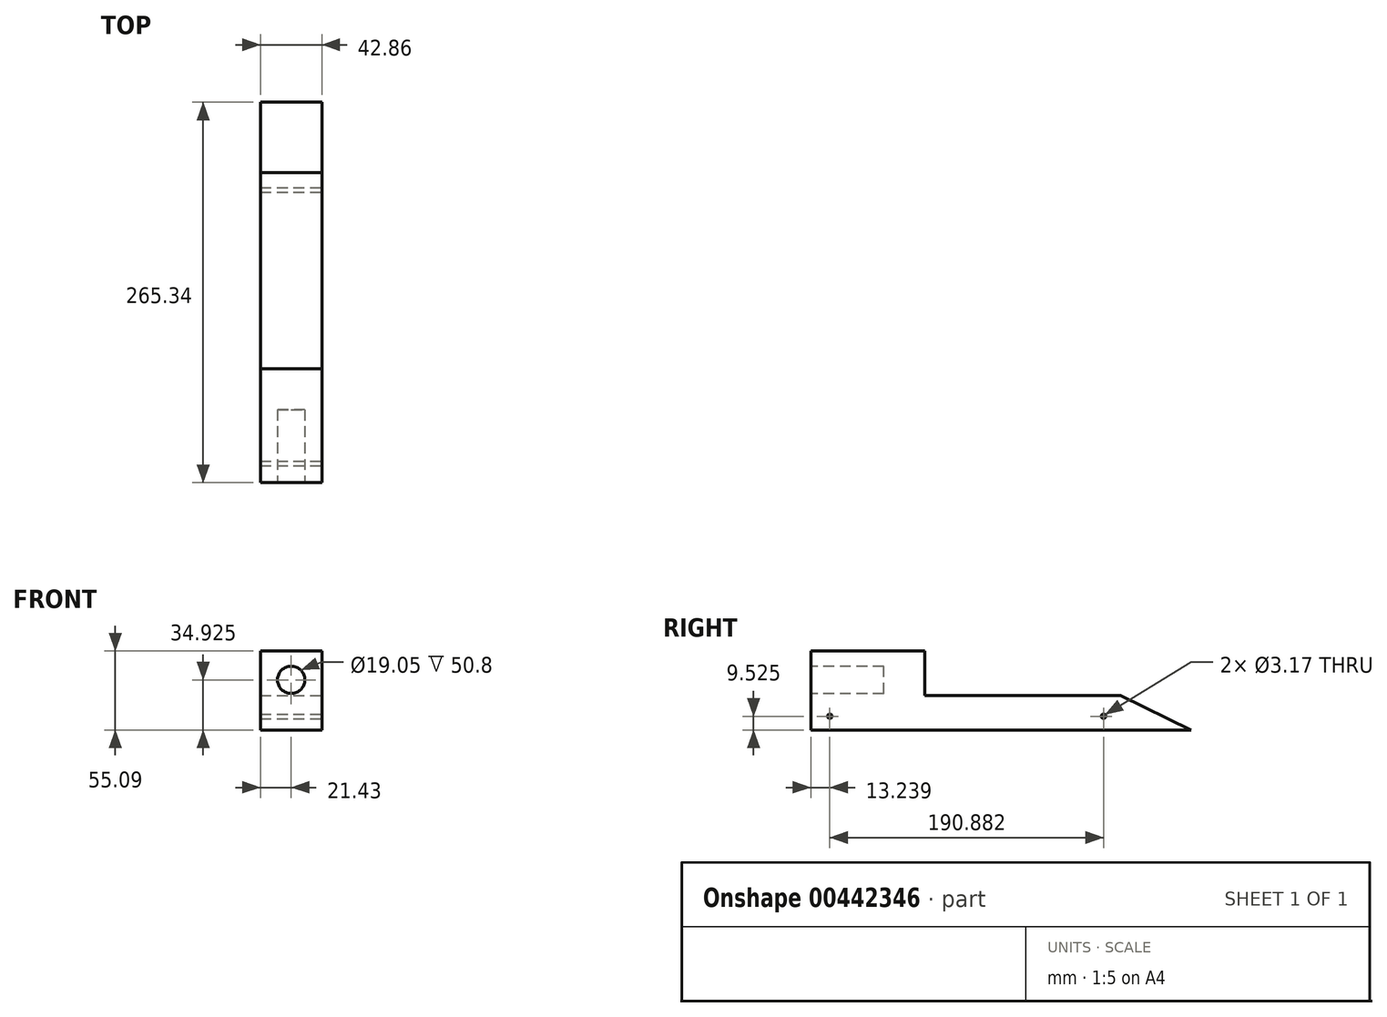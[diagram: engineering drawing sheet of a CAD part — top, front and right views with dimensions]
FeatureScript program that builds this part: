
annotation { "Feature Type Name" : "Feature", "Feature Type Description" : "" }
export const myFeature = defineFeature(function(context is Context, id is Id, definition is map)
    precondition{}
    {
        {
            var Q0;
            Q0=qCreatedBy(makeId("Right.planeOp"),FACE);
            var sketch = newSketch(context, id + "F0", { "sketchPlane" : qUnion([Q0])});
            skLineSegment(sketch, "E0", {"start": v(-152.4, 0) * mm, "end": v(152.4, 0) * mm});
            skLineSegment(sketch, "E1", {"start": v(-152.4, 0) * mm, "end": v(-152.4, 69.85) * mm});
            skLineSegment(sketch, "E2", {"start": v(152.4, 0) * mm, "end": v(152.4, 19.05) * mm});
            skLineSegment(sketch, "E3", {"start": v(152.4, 19.05) * mm, "end": v(-152.4, 69.85) * mm});
            skPoint(sketch, "E4.endSnap0", {"position": v(-152.4, 34.93) * mm});
            skLineSegment(sketch, "E5.0", {"start": v(-95.25, 50.8) * mm, "end": v(-152.4, 50.8) * mm, "construction": true});
            skLineSegment(sketch, "E5.1", {"start": v(-95.25, 50.8) * mm, "end": v(-95.25, 19.05) * mm, "construction": true});
            skLineSegment(sketch, "E5.2", {"start": v(-95.25, 19.05) * mm, "end": v(-152.4, 19.05) * mm, "construction": true});
            skSolve(sketch);
        }
        {
            var Q0;
            Q0=makeQuery(id+"F0.imprint","IMPRINT",FACE,{"disambiguationData":[TD([[makeQuery(id+"F0.imprint","IMPRINT",EDGE,{"derivedFrom":sQuery(id+"F0.wireOp",EDGE,"E0")}),1.0]])]});
            extrude(context, id + "F1", {"entities" : qUnion([Q0]), "depth" : 42.86 * mm, "symmetric" : true});
        }
        {
            var Q0;
            Q0=makeQuery(id+"F1.opExtrude","SWEPT_FACE",FACE,{"disambiguationData":[OSD([sQuery(id+"F0.wireOp",EDGE,"E1")])]});
            var sketch = newSketch(context, id + "F2", { "sketchPlane" : qUnion([Q0])});
            skLineSegment(sketch, "E6", {"start": v(21.43, 34.93) * mm, "end": v(0, 34.93) * mm, "construction": true});
            skCircle(sketch, "E7", {"center": v(0, 34.93) * mm, "radius": 9.53 * mm});
            skSolve(sketch);
        }
        {
            var Q0;
            Q0=makeQuery(id+"F2.imprint","IMPRINT",FACE,{"disambiguationData":[TD([[makeQuery(id+"F2.imprint","IMPRINT",EDGE,{"derivedFrom":sQuery(id+"F2.wireOp",EDGE,"E7")}),1.0]])]});
            var Q1;
            Q1=sQuery(id+"F2.wireOp",EDGE,"E7");
            extrude(context, id + "F3", {"entities" : qUnion([Q0]), "operationType" : NewBodyOperationType.REMOVE, "surfaceEntities" : qUnion([Q1]), "oppositeDirection" : true, "depth" : 50.8 * mm});
        }
        {
            var Q0;
            Q0=makeQuery(id+"F1.opExtrude","CAP_FACE",FACE,{"disambiguationData":[OSD([sQuery(id+"F0.wireOp",EDGE,"E0"),sQuery(id+"F0.wireOp",EDGE,"E1"),sQuery(id+"F0.wireOp",EDGE,"E2"),sQuery(id+"F0.wireOp",EDGE,"E3")])],"isStart":false});
            var sketch = newSketch(context, id + "F4", { "sketchPlane" : qUnion([Q0])});
            skLineSegment(sketch, "E8", {"start": v(-152.4, 34.93) * mm, "end": v(-152.4, 44.45) * mm, "construction": true});
            skLineSegment(sketch, "E9.0", {"start": v(-95.25, 19.05) * mm, "end": v(-152.4, 19.05) * mm, "construction": true});
            skLineSegment(sketch, "E9.1", {"start": v(-95.25, 50.8) * mm, "end": v(-95.25, 19.05) * mm, "construction": true});
            skLineSegment(sketch, "E9.2", {"start": v(-152.4, 50.8) * mm, "end": v(-95.25, 50.8) * mm, "construction": true});
            skLineSegment(sketch, "E10", {"start": v(57.15, 0) * mm, "end": v(57.15, 34.93) * mm, "construction": true});
            skLineSegment(sketch, "E11", {"start": v(-152.4, 44.45) * mm, "end": v(-101.6, 44.45) * mm, "construction": true});
            skLineSegment(sketch, "E12", {"start": v(-101.6, 44.45) * mm, "end": v(-101.6, 25.4) * mm, "construction": true});
            skLineSegment(sketch, "E13", {"start": v(-101.6, 25.4) * mm, "end": v(-152.4, 25.4) * mm, "construction": true});
            skLineSegment(sketch, "E14", {"start": v(-152.4, 55.1) * mm, "end": v(-73, 55.1) * mm});
            skLineSegment(sketch, "E15", {"start": v(-73, 37.35) * mm, "end": v(-73, 24.03) * mm});
            skLineSegment(sketch, "E16", {"start": v(-73, 24.03) * mm, "end": v(63.73, 24.03) * mm});
            skLineSegment(sketch, "E17", {"start": v(63.73, 24.03) * mm, "end": v(112.94, 0) * mm});
            skCircle(sketch, "E18", {"center": v(-139.16, 9.53) * mm, "radius": 1.59 * mm});
            skCircle(sketch, "E19", {"center": v(51.72, 9.53) * mm, "radius": 1.59 * mm});
            skLineSegment(sketch, "E20", {"start": v(-73, 55.1) * mm, "end": v(-73, 37.35) * mm});
            skSolve(sketch);
        }
        {
            var Q0;
            {var subQ3=sQuery(id+"F4.wireOp",EDGE,"E14");Q0=makeQuery(id+"F4.imprint","IMPRINT",FACE,{"disambiguationData":[TD([[makeQuery(id+"F4.imprint","IMPRINT",EDGE,{"derivedFrom":subQ3}),-1.0]])]});}
            extrude(context, id + "F5", {"entities" : qUnion([Q0]), "operationType" : NewBodyOperationType.INTERSECT, "endBound" : BoundingType.THROUGH_ALL, "oppositeDirection" : true, "depth" : 25.4 * mm});
        }
    });
